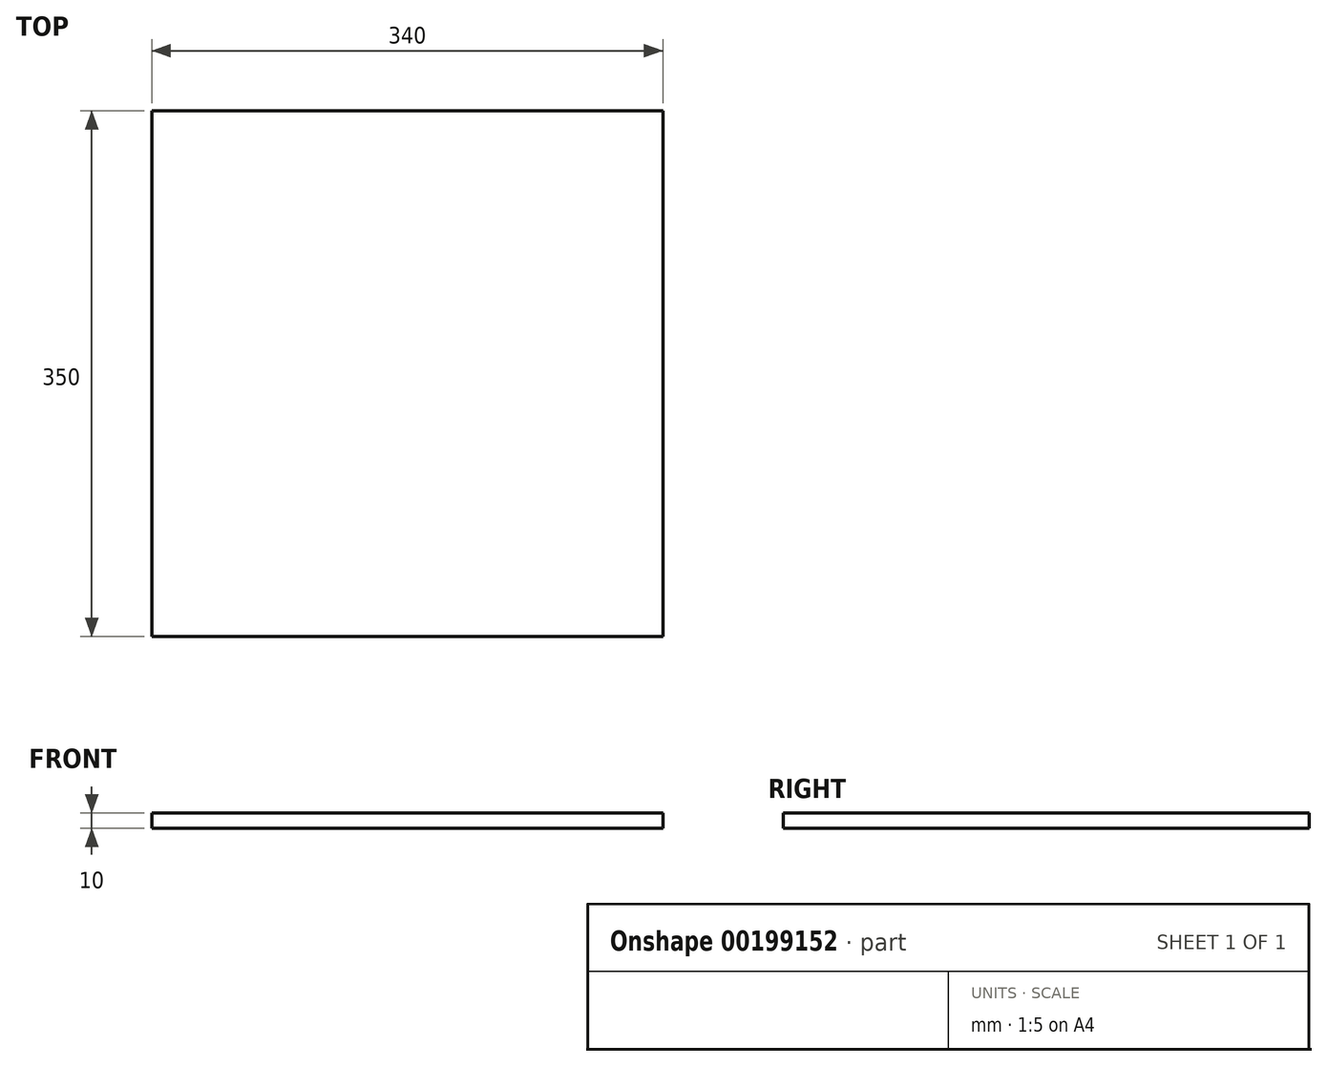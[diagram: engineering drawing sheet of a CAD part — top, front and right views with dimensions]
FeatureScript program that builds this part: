
annotation { "Feature Type Name" : "Feature", "Feature Type Description" : "" }
export const myFeature = defineFeature(function(context is Context, id is Id, definition is map)
    precondition{}
    {
        {
            var Q0;
            Q0=qCreatedBy(makeId("Top.planeOp"),FACE);
            var sketch = newSketch(context, id + "F0", { "sketchPlane" : qUnion([Q0])});
            skLineSegment(sketch, "E0.bottom", {"start": v(-44.88, 208.19) * mm, "end": v(295.12, 208.19) * mm});
            skLineSegment(sketch, "E0.top", {"start": v(-44.88, -141.81) * mm, "end": v(295.12, -141.81) * mm});
            skLineSegment(sketch, "E0.left", {"start": v(-44.88, 208.19) * mm, "end": v(-44.88, -141.81) * mm});
            skLineSegment(sketch, "E0.right", {"start": v(295.12, 208.19) * mm, "end": v(295.12, -141.81) * mm});
            skSolve(sketch);
        }
        {
            var Q0;
            Q0=qSketchRegion(id+"F0",true);
            extrude(context, id + "F1", {"entities" : qUnion([Q0]), "depth" : 10 * mm});
        }
    });
